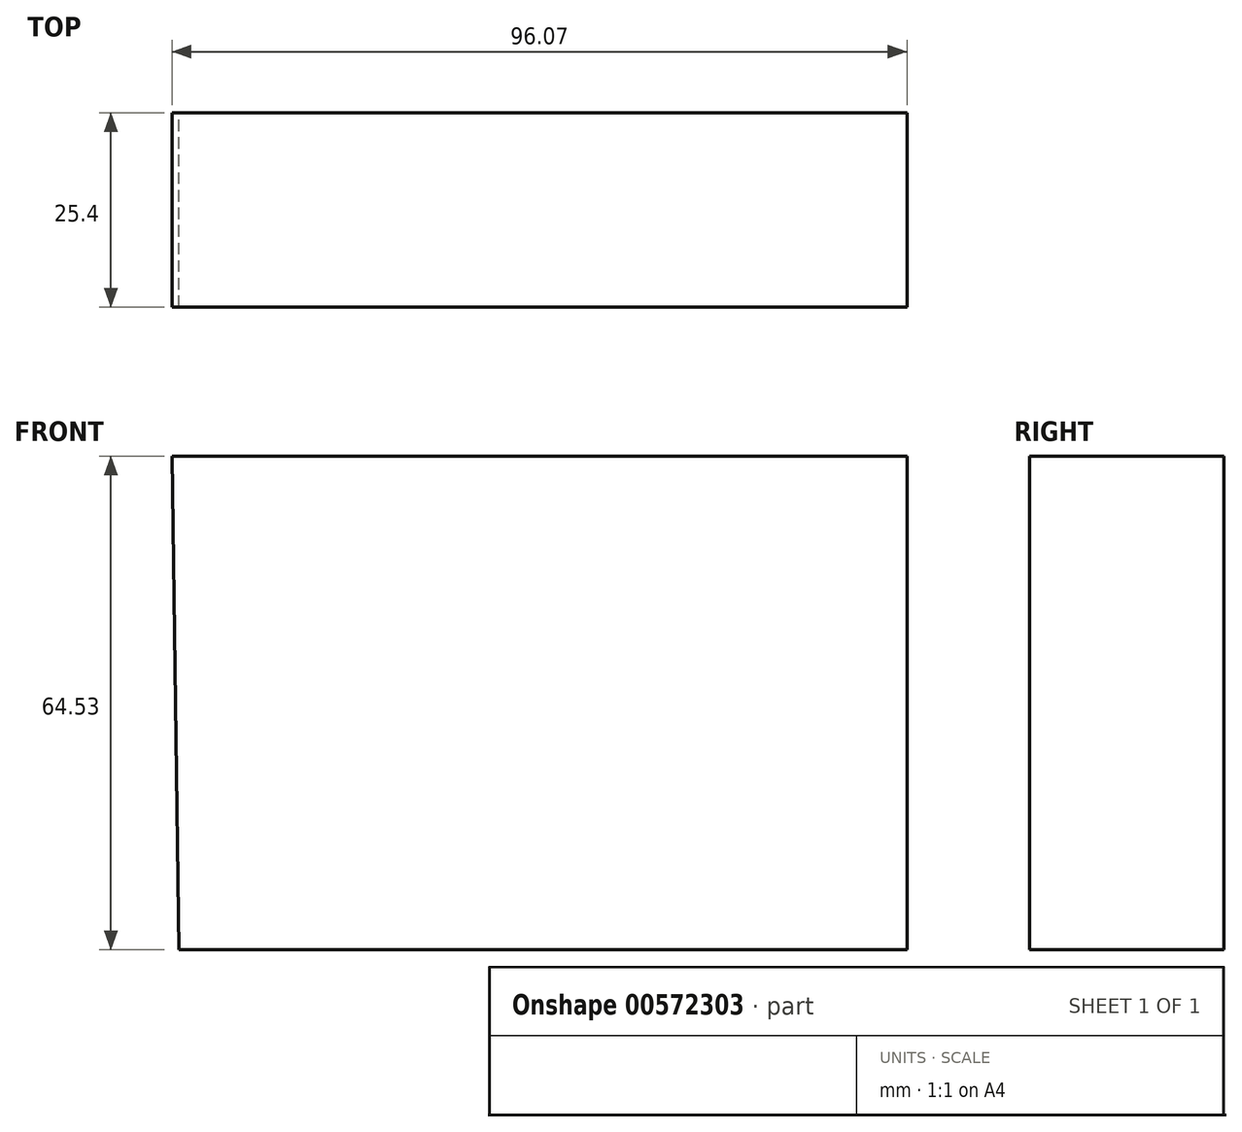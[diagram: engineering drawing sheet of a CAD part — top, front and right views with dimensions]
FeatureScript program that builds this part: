
annotation { "Feature Type Name" : "Feature", "Feature Type Description" : "" }
export const myFeature = defineFeature(function(context is Context, id is Id, definition is map)
    precondition{}
    {
        {
            var Q0;
            Q0=qCreatedBy(makeId("Front.planeOp"),FACE);
            var sketch = newSketch(context, id + "F0", { "sketchPlane" : qUnion([Q0])});
            skLineSegment(sketch, "E0", {"start": v(-52.27, 48.18) * mm, "end": v(43.8, 48.18) * mm});
            skLineSegment(sketch, "E1", {"start": v(43.8, 48.18) * mm, "end": v(43.8, -16.35) * mm});
            skLineSegment(sketch, "E2", {"start": v(43.8, -16.35) * mm, "end": v(-51.4, -16.35) * mm});
            skLineSegment(sketch, "E3", {"start": v(-51.4, -16.35) * mm, "end": v(-52.27, 48.18) * mm});
            skSolve(sketch);
        }
        {
            var Q0;
            Q0=makeQuery(id+"F0.imprint","IMPRINT",FACE,{"disambiguationData":[TD([[makeQuery(id+"F0.imprint","IMPRINT",EDGE,{"derivedFrom":sQuery(id+"F0.wireOp",EDGE,"E0")}),-1.0]])]});
            extrude(context, id + "F1", {"entities" : qUnion([Q0]), "depth" : 25.4 * mm, "offsetDistance" : 25.4 * mm});
        }
    });
